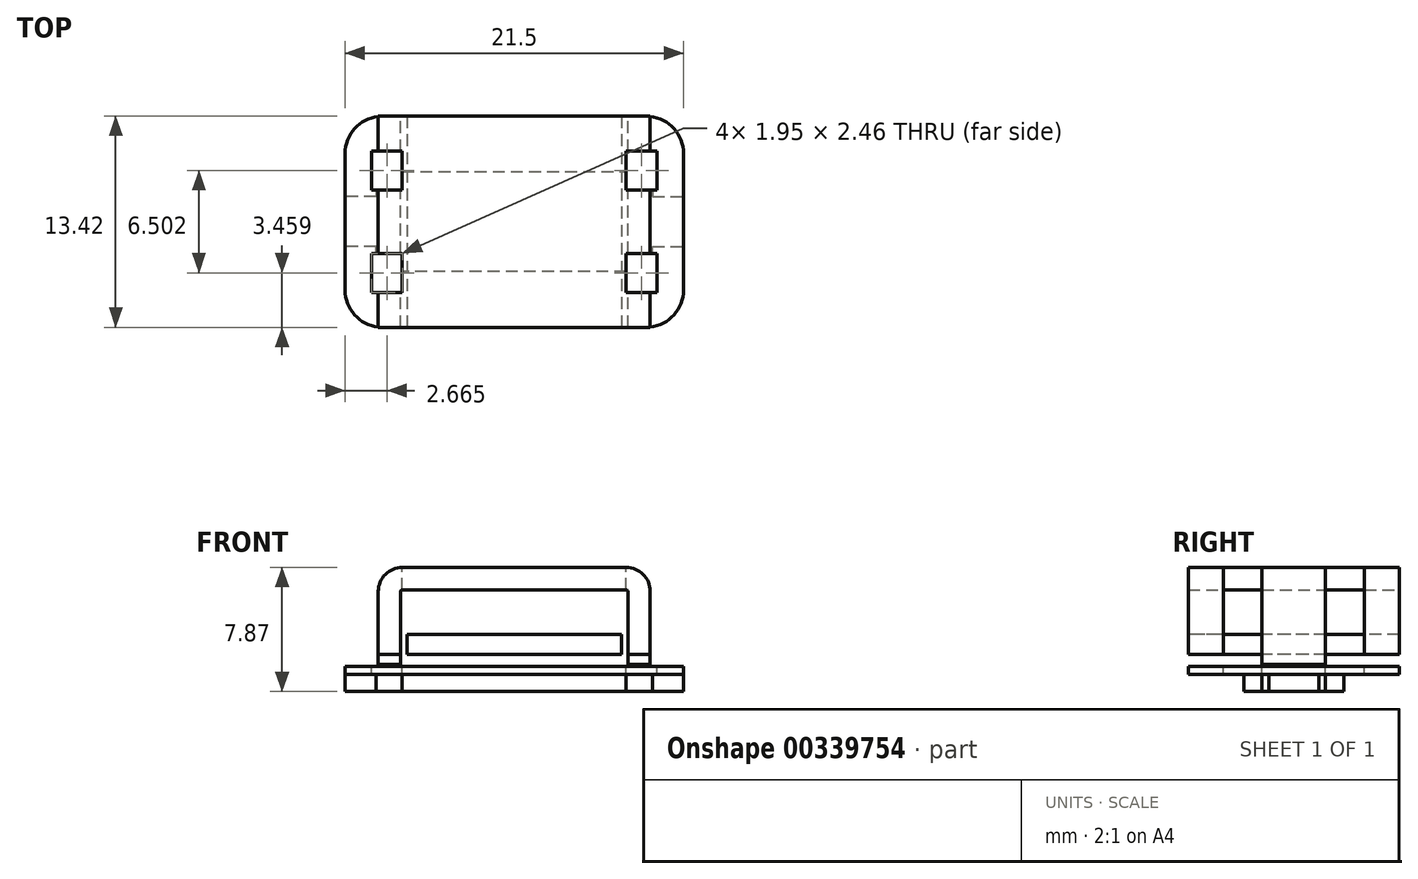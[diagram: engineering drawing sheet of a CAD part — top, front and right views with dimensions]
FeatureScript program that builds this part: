
annotation { "Feature Type Name" : "Feature", "Feature Type Description" : "" }
export const myFeature = defineFeature(function(context is Context, id is Id, definition is map)
    precondition{}
    {
        {
            var Q0;
            Q0=qCreatedBy(makeId("Top.planeOp"),FACE);
            var sketch = newSketch(context, id + "F0", { "sketchPlane" : qUnion([Q0])});
            skLineSegment(sketch, "E0", {"start": v(0, 3.18) * mm, "end": v(-8.78, 3.17) * mm});
            skLineSegment(sketch, "E1", {"start": v(-8.78, 3.17) * mm, "end": v(-8.78, 1.59) * mm});
            skLineSegment(sketch, "E2", {"start": v(-8.78, 1.59) * mm, "end": v(-10.75, 1.59) * mm});
            skLineSegment(sketch, "E3", {"start": v(-10.75, 1.59) * mm, "end": v(-10.75, 0) * mm});
            skLineSegment(sketch, "E4", {"start": v(-10.75, 0) * mm, "end": v(0, 0) * mm, "construction": true});
            skLineSegment(sketch, "E5", {"start": v(0, 0) * mm, "end": v(0, 3.18) * mm, "construction": true});
            skLineSegment(sketch, "E6.MirrorCS", {"start": v(0, 3.18) * mm, "end": v(8.78, 3.17) * mm});
            skLineSegment(sketch, "E7.MirrorCS", {"start": v(8.78, 3.17) * mm, "end": v(8.78, 1.59) * mm});
            skLineSegment(sketch, "E8.MirrorCS", {"start": v(8.78, 1.59) * mm, "end": v(10.75, 1.59) * mm});
            skLineSegment(sketch, "E9.MirrorCS", {"start": v(10.75, 1.59) * mm, "end": v(10.75, 0) * mm});
            skLineSegment(sketch, "E10.MirrorCS", {"start": v(-10.75, -1.59) * mm, "end": v(-10.75, 0) * mm});
            skLineSegment(sketch, "E11.MirrorCS", {"start": v(-8.78, -1.59) * mm, "end": v(-10.75, -1.59) * mm});
            skLineSegment(sketch, "E12.MirrorCS", {"start": v(-8.78, -3.17) * mm, "end": v(-8.78, -1.59) * mm});
            skLineSegment(sketch, "E13.MirrorCS", {"start": v(0, -3.18) * mm, "end": v(-8.78, -3.17) * mm});
            skLineSegment(sketch, "E14.MirrorCS", {"start": v(8.78, -3.17) * mm, "end": v(8.78, -1.59) * mm});
            skLineSegment(sketch, "E15.MirrorCS", {"start": v(8.78, -1.59) * mm, "end": v(10.75, -1.59) * mm});
            skLineSegment(sketch, "E16.MirrorCS", {"start": v(10.75, -1.59) * mm, "end": v(10.75, 0) * mm});
            skLineSegment(sketch, "E17.MirrorCS", {"start": v(0, -3.18) * mm, "end": v(8.78, -3.17) * mm});
            skSolve(sketch);
        }
        {
            var Q0;
            Q0 = qSketchRegion(id + "F0", true);
            extrude(context, id + "F1", {"entities" : qUnion([Q0]), "depth" : 1.1 * mm});
        }
        {
            var Q0;
            Q0=makeQuery(id+"F1.opExtrude","CAP_FACE",FACE,{"disambiguationData":[OSD([sQuery(id+"F0.wireOp",EDGE,"E0"),sQuery(id+"F0.wireOp",EDGE,"E1"),sQuery(id+"F0.wireOp",EDGE,"E2"),sQuery(id+"F0.wireOp",EDGE,"E3"),sQuery(id+"F0.wireOp",EDGE,"E6.MirrorCS"),sQuery(id+"F0.wireOp",EDGE,"E7.MirrorCS"),sQuery(id+"F0.wireOp",EDGE,"E8.MirrorCS"),sQuery(id+"F0.wireOp",EDGE,"E9.MirrorCS"),sQuery(id+"F0.wireOp",EDGE,"E10.MirrorCS"),sQuery(id+"F0.wireOp",EDGE,"E11.MirrorCS"),sQuery(id+"F0.wireOp",EDGE,"E12.MirrorCS"),sQuery(id+"F0.wireOp",EDGE,"E13.MirrorCS"),sQuery(id+"F0.wireOp",EDGE,"E14.MirrorCS"),sQuery(id+"F0.wireOp",EDGE,"E15.MirrorCS"),sQuery(id+"F0.wireOp",EDGE,"E16.MirrorCS"),sQuery(id+"F0.wireOp",EDGE,"E17.MirrorCS")])],"isStart":false});
            var sketch = newSketch(context, id + "F2", { "sketchPlane" : qUnion([Q0])});
            skLineSegment(sketch, "E18.bottom", {"start": v(-10.75, 6.7) * mm, "end": v(10.75, 6.7) * mm});
            skLineSegment(sketch, "E18.top", {"start": v(-10.75, -6.7) * mm, "end": v(10.75, -6.7) * mm});
            skLineSegment(sketch, "E18.left", {"start": v(-10.75, 6.7) * mm, "end": v(-10.75, -6.7) * mm});
            skLineSegment(sketch, "E18.right", {"start": v(10.75, 6.7) * mm, "end": v(10.75, -6.7) * mm});
            skPoint(sketch, "E18.middle", {"position": v(0, 0) * mm});
            skSolve(sketch);
        }
        {
            var Q0;
            Q0 = qSketchRegion(id + "F2", true);
            extrude(context, id + "F3", {"entities" : qUnion([Q0]), "depth" : 0.5 * mm});
        }
        {
            var Q0;
            Q0=makeQuery(id+"F3.opExtrude","SWEPT_EDGE",EDGE,{"disambiguationData":[OSD([sQuery(id+"F2.wireOp",EDGE,"E18.top"),sQuery(id+"F2.wireOp",EDGE,"E18.right")])]});
            var Q1;
            Q1=makeQuery(id+"F3.opExtrude","SWEPT_EDGE",EDGE,{"disambiguationData":[OSD([sQuery(id+"F2.wireOp",EDGE,"E18.bottom"),sQuery(id+"F2.wireOp",EDGE,"E18.right")])]});
            var Q2;
            Q2=makeQuery(id+"F3.opExtrude","SWEPT_EDGE",EDGE,{"disambiguationData":[OSD([sQuery(id+"F2.wireOp",EDGE,"E18.top"),sQuery(id+"F2.wireOp",EDGE,"E18.left")])]});
            var Q3;
            Q3=makeQuery(id+"F3.opExtrude","SWEPT_EDGE",EDGE,{"disambiguationData":[OSD([sQuery(id+"F2.wireOp",EDGE,"E18.bottom"),sQuery(id+"F2.wireOp",EDGE,"E18.left")])]});
            fillet(context, id + "F4", {"entities" : qUnion([Q0, Q1, Q2, Q3]), "radius" : 2.38 * mm, "tangentPropagation" : true, "allowEdgeOverflow" : false});
        }
        {
            var Q0;
            Q0=qCreatedBy(makeId("Front.planeOp"),FACE);
            var sketch = newSketch(context, id + "F5", { "sketchPlane" : qUnion([Q0])});
            skLineSegment(sketch, "E19", {"start": v(0, 0) * mm, "end": v(0, 7.87) * mm, "construction": true});
            skLineSegment(sketch, "E20", {"start": v(0, 7.87) * mm, "end": v(-7.11, 7.87) * mm});
            skLineSegment(sketch, "E21", {"start": v(-8.64, 6.35) * mm, "end": v(-8.64, 2.36) * mm});
            skPoint(sketch, "E22.visualSharp", {"position": v(-8.64, 7.87) * mm});
            skArc(sketch, "E22.filletArc", {"start": v(-7.11, 7.87) * mm, "mid": v(-8.19, 7.43) * mm, "end": v(-8.64, 6.35) * mm});
            skLineSegment(sketch, "E23.MirrorCS", {"start": v(0, 7.87) * mm, "end": v(7.11, 7.87) * mm});
            skArc(sketch, "E24.MirrorCS", {"start": v(7.11, 7.87) * mm, "mid": v(8.19, 7.43) * mm, "end": v(8.64, 6.35) * mm});
            skLineSegment(sketch, "E25.MirrorCS", {"start": v(8.64, 6.35) * mm, "end": v(8.64, 2.36) * mm});
            skLineSegment(sketch, "E26.0", {"start": v(-7.21, 6.35) * mm, "end": v(-7.21, 2.36) * mm});
            skArc(sketch, "E26.1", {"start": v(-7.11, 6.45) * mm, "mid": v(-7.18, 6.42) * mm, "end": v(-7.21, 6.35) * mm});
            skLineSegment(sketch, "E26.2", {"start": v(7.21, 6.35) * mm, "end": v(7.21, 2.36) * mm});
            skArc(sketch, "E26.3", {"start": v(7.11, 6.45) * mm, "mid": v(7.18, 6.42) * mm, "end": v(7.21, 6.35) * mm});
            skLineSegment(sketch, "E26.4", {"start": v(0, 6.45) * mm, "end": v(7.11, 6.45) * mm});
            skLineSegment(sketch, "E26.5", {"start": v(0, 6.45) * mm, "end": v(-7.11, 6.45) * mm});
            skLineSegment(sketch, "E27", {"start": v(-8.64, 2.36) * mm, "end": v(-7.21, 2.36) * mm});
            skLineSegment(sketch, "E28", {"start": v(8.64, 2.36) * mm, "end": v(7.21, 2.36) * mm});
            skSolve(sketch);
        }
        {
            var Q0;
            Q0 = qSketchRegion(id + "F5", true);
            var Q1;
            Q1=makeQuery(id+"F3.opExtrude","SWEPT_FACE",FACE,{"disambiguationData":[OSD([sQuery(id+"F2.wireOp",EDGE,"E18.top")])]});
            var Q2;
            Q2=makeQuery(id+"F3.opExtrude","SWEPT_FACE",FACE,{"disambiguationData":[OSD([sQuery(id+"F2.wireOp",EDGE,"E18.bottom")])]});
            extrude(context, id + "F6", {"entities" : qUnion([Q0]), "endBound" : BoundingType.UP_TO_SURFACE, "endBoundEntityFace" : qUnion([Q1]), "depth" : 25.4 * mm, "hasSecondDirection" : true, "secondDirectionBound" : SecondDirectionBoundingType.UP_TO_SURFACE, "secondDirectionOppositeDirection" : true, "secondDirectionBoundEntityFace" : qUnion([Q2]), "secondDirectionDepth" : 25.4 * mm});
        }
        {
            var Q0;
            Q0=makeQuery(id+"F6.opExtrude","SWEPT_FACE",FACE,{"disambiguationData":[OSD([sQuery(id+"F5.wireOp",EDGE,"E27")])]});
            var sketch = newSketch(context, id + "F7", { "sketchPlane" : qUnion([Q0])});
            skLineSegment(sketch, "E29.bottom", {"start": v(-6.82, -6.7) * mm, "end": v(6.82, -6.7) * mm});
            skLineSegment(sketch, "E29.top", {"start": v(-6.82, 6.7) * mm, "end": v(6.82, 6.7) * mm});
            skLineSegment(sketch, "E29.left", {"start": v(-6.82, -6.7) * mm, "end": v(-6.82, 6.7) * mm});
            skLineSegment(sketch, "E29.right", {"start": v(6.82, -6.7) * mm, "end": v(6.82, 6.7) * mm});
            skPoint(sketch, "E29.middle", {"position": v(0, 0) * mm});
            skSolve(sketch);
        }
        {
            var Q0;
            Q0 = qSketchRegion(id + "F7", true);
            extrude(context, id + "F8", {"entities" : qUnion([Q0]), "oppositeDirection" : true, "depth" : 1.27 * mm});
        }
        {
            var Q0;
            Q0=makeQuery(id+"F6.opExtrude","SWEPT_FACE",FACE,{"disambiguationData":[OSD([sQuery(id+"F5.wireOp",EDGE,"E20"),sQuery(id+"F5.wireOp",EDGE,"E23.MirrorCS")])]});
            var sketch = newSketch(context, id + "F9", { "sketchPlane" : qUnion([Q0])});
            skLineSegment(sketch, "E30.bottom", {"start": v(-7.11, 4.48) * mm, "end": v(-9.06, 4.48) * mm});
            skLineSegment(sketch, "E30.top", {"start": v(-7.11, 2.02) * mm, "end": v(-9.06, 2.02) * mm});
            skLineSegment(sketch, "E30.left", {"start": v(-7.11, 4.48) * mm, "end": v(-7.11, 2.02) * mm});
            skLineSegment(sketch, "E30.right", {"start": v(-9.06, 4.48) * mm, "end": v(-9.06, 2.02) * mm});
            skLineSegment(sketch, "E31", {"start": v(0, 0) * mm, "end": v(-7.11, 0) * mm, "construction": true});
            skLineSegment(sketch, "E32", {"start": v(0, 0) * mm, "end": v(0, 6.7) * mm, "construction": true});
            skLineSegment(sketch, "E33.MirrorCS", {"start": v(-7.11, -2.02) * mm, "end": v(-9.06, -2.02) * mm});
            skLineSegment(sketch, "E34.MirrorCS", {"start": v(-7.11, -4.48) * mm, "end": v(-7.11, -2.02) * mm});
            skLineSegment(sketch, "E35.MirrorCS", {"start": v(-7.11, -4.48) * mm, "end": v(-9.06, -4.48) * mm});
            skLineSegment(sketch, "E36.MirrorCS", {"start": v(-9.06, -4.48) * mm, "end": v(-9.06, -2.02) * mm});
            skLineSegment(sketch, "E37.MirrorCS", {"start": v(7.11, 4.48) * mm, "end": v(9.06, 4.48) * mm});
            skLineSegment(sketch, "E38.MirrorCS", {"start": v(9.06, 4.48) * mm, "end": v(9.06, 2.02) * mm});
            skLineSegment(sketch, "E39.MirrorCS", {"start": v(7.11, 4.48) * mm, "end": v(7.11, 2.02) * mm});
            skLineSegment(sketch, "E40.MirrorCS", {"start": v(7.11, 2.02) * mm, "end": v(9.06, 2.02) * mm});
            skLineSegment(sketch, "E41.MirrorCS", {"start": v(7.11, -2.02) * mm, "end": v(9.06, -2.02) * mm});
            skLineSegment(sketch, "E42.MirrorCS", {"start": v(7.11, -4.48) * mm, "end": v(7.11, -2.02) * mm});
            skLineSegment(sketch, "E43.MirrorCS", {"start": v(7.11, -4.48) * mm, "end": v(9.06, -4.48) * mm});
            skLineSegment(sketch, "E44.MirrorCS", {"start": v(9.06, -4.48) * mm, "end": v(9.06, -2.02) * mm});
            skSolve(sketch);
        }
        {
            var Q0;
            Q0 = qSketchRegion(id + "F9", true);
            extrude(context, id + "F10", {"entities" : qUnion([Q0]), "operationType" : NewBodyOperationType.REMOVE, "endBound" : BoundingType.THROUGH_ALL, "oppositeDirection" : true, "depth" : 25.4 * mm});
        }
        {
            var Q0;
            Q0=makeQuery(id+"F10.boolean.opBoolean","SPLIT",FACE,{"disambiguationData":[TD([makeQuery(id+"F10.opExtrude","SWEPT_FACE",FACE,{"disambiguationData":[OSD([sQuery(id+"F9.wireOp",EDGE,"E30.top")])]})])],"derivedFrom":makeQuery(id+"F6.opExtrude","SWEPT_FACE",FACE,{"disambiguationData":[OSD([sQuery(id+"F5.wireOp",EDGE,"E27")])]})});
            var sketch = newSketch(context, id + "F11", { "sketchPlane" : qUnion([Q0])});
            skLineSegment(sketch, "E45.1", {"start": v(-8.64, 2.02) * mm, "end": v(-8.64, -2.02) * mm});
            skLineSegment(sketch, "E46.0", {"start": v(-7.21, -2.02) * mm, "end": v(-8.64, -2.02) * mm});
            skLineSegment(sketch, "E46.1", {"start": v(-7.21, 2.02) * mm, "end": v(-7.21, -2.02) * mm});
            skLineSegment(sketch, "E46.2", {"start": v(-7.21, 2.02) * mm, "end": v(-8.64, 2.02) * mm});
            skLineSegment(sketch, "E47.0", {"start": v(8.64, 2.02) * mm, "end": v(7.21, 2.02) * mm});
            skLineSegment(sketch, "E47.1", {"start": v(8.64, -2.02) * mm, "end": v(7.21, -2.02) * mm});
            skLineSegment(sketch, "E47.2", {"start": v(8.64, 2.02) * mm, "end": v(8.64, -2.02) * mm});
            skLineSegment(sketch, "E47.3", {"start": v(7.21, 2.02) * mm, "end": v(7.21, -2.02) * mm});
            skPoint(sketch, "E47.4", {"position": v(7.21, 0) * mm});
            skSolve(sketch);
        }
        {
            var Q0;
            Q0 = qSketchRegion(id + "F11", true);
            extrude(context, id + "F12", {"entities" : qUnion([Q0]), "operationType" : NewBodyOperationType.ADD, "depth" : 0.64 * mm});
        }
    });
